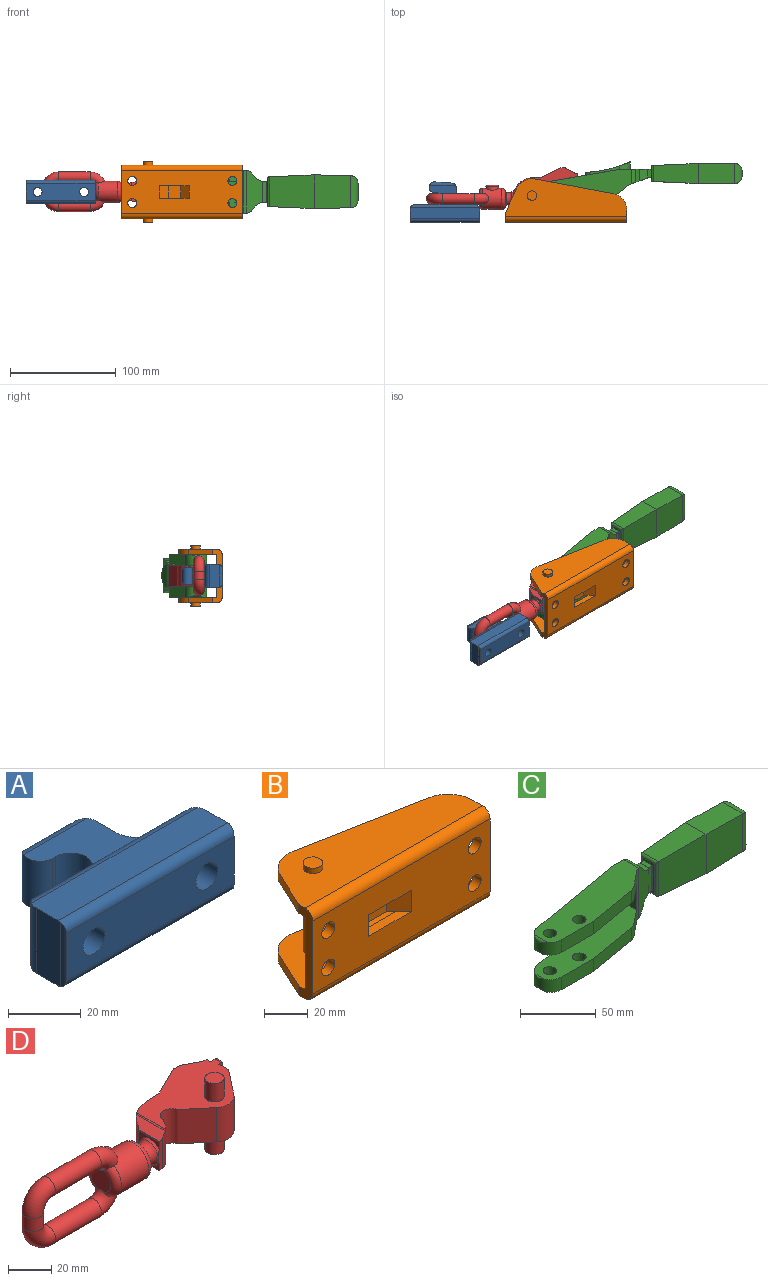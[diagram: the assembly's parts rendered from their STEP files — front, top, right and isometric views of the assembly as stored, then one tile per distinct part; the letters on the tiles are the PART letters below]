
ASSEMBLY  parts=4 mates=3
PART A: 33 faces, bbox 66x38x22 mm
  f0: cylinder r=5mm len=16mm, axis (0,0,1), area 241.4mm2, adj f1,f20,f24,f28,f29,f30
  f1: cylinder r=3mm len=24.58mm, axis (1,0,0), area 67.6mm2, adj f0,f2,f20,f30
  f2: cylinder r=5mm len=16mm, axis (0,0,1), area 117.4mm2, adj f1,f20,f23,f28,f29,f30
  f3: cylinder r=3mm len=64.66mm, axis (1,0,0), area 220mm2, adj f4,f7,f9,f14,f15,f25,f26,f30
  f4: cylinder r=8mm len=19.32mm, axis (0,0,1), area 172.4mm2, adj f3,f5,f15,f16,f22,f23,f28,f30
  f5: cylinder r=3mm len=64.66mm, axis (1,0,0), area 220mm2, adj f4,f8,f9,f14,f22,f25,f26,f28
  f6: cylinder r=3mm len=66mm, axis (1,0,0), area 309.5mm2, adj f7,f10,f11,f12,f13,f21
  f7: plane 66x11mm, normal (0,0,1), area 724.9mm2, adj f3,f6,f9,f12,f13,f14
  f8: plane 66x11mm, normal (0,0,-1), area 724.9mm2, adj f5,f9,f12,f13,f14,f27
  f9: cylinder r=5mm len=22mm, axis (0,0,1), area 162.6mm2, adj f3,f5,f7,f8,f13,f19,f26
  f10: cylinder r=5mm len=21.66mm, axis (0,0,1), area 38.7mm2, adj f6,f11,f13,f27
  f11: plane 65.17x16mm, normal (0,-1,0), area 929.2mm2, adj f6,f10,f17,f21,f27,f31
  f12: plane 22x9.5mm, normal (1,0,0), area 208.9mm2, adj f6,f7,f8,f14,f21,f27
  f13: plane 22x9.5mm, normal (-1,0,0), area 208.9mm2, adj f6,f7,f8,f9,f10,f27
  f14: cylinder r=5mm len=22mm, axis (0,0,1), area 162.6mm2, adj f3,f5,f7,f8,f12,f15,f16,f22
  f15: plane 9x6.57mm, normal (0,1,0), area 33.1mm2, adj f3,f4,f14,f16
  f16: cylinder r=6.75mm len=13.5mm, axis (0,1,0), area 381.7mm2, adj f4,f14,f15,f22,f32
  f17: cylinder r=4.25mm len=8.5mm, axis (0,1,0), area 200.3mm2, adj f11,f18
  f18: plane 13.5x13.5mm, normal (0,1,0), area 86.4mm2, adj f17,f19
  f19: cylinder r=6.75mm len=13.5mm, axis (0,1,0), area 381.7mm2, adj f9,f18,f26
  f20: plane 16x14.49mm, normal (0.06,1,0), area 210.6mm2, adj f0,f1,f2,f29
  f21: cylinder r=5mm len=21.66mm, axis (0,0,1), area 38.7mm2, adj f6,f11,f12,f27
  f22: plane 9x6.57mm, normal (0,1,0), area 33.1mm2, adj f4,f5,f14,f16
  f23: plane 16x7.5mm, normal (1,0,0), area 120mm2, adj f2,f4,f28,f30
  f24: plane 16x1mm, normal (0,-1,0), area 16mm2, adj f0,f25,f28,f30
  f25: cylinder r=6mm len=19.32mm, axis (0,0,1), area 263.9mm2, adj f3,f5,f24,f26,f28,f30
  f26: plane 21.4x19.32mm, normal (0,1,0), area 273.3mm2, adj f3,f5,f9,f19,f25
  f27: cylinder r=3mm len=66mm, axis (1,0,0), area 309.5mm2, adj f8,f10,f11,f12,f13,f21
  f28: plane 31.22x18mm, normal (0,0,-1), area 351.8mm2, adj f0,f2,f4,f5,f23,f24,f25,f29
  f29: cylinder r=3mm len=24.58mm, axis (1,0,0), area 67.6mm2, adj f0,f2,f20,f28
  f30: plane 31.22x18mm, normal (0,0,1), area 351.8mm2, adj f0,f1,f2,f3,f4,f23,f24,f25
  f31: cylinder r=4.25mm len=8.5mm, axis (0,1,0), area 200.3mm2, adj f11,f32
  f32: plane 13.5x13.5mm, normal (0,1,0), area 86.4mm2, adj f16,f31
PART B: 41 faces, bbox 115x41x57 mm
  f0: plane 27.86x5mm, normal (0,0,1), area 114.3mm2, adj f16,f25,f32,f34
  f1: cylinder r=4.5mm len=41mm, axis (0,0,1), area 1159.2mm2, adj f28,f30
  f2: plane 27.86x5mm, normal (0,0,-1), area 114.3mm2, adj f16,f25,f32,f34
  f3: plane 22.55x10.49mm, normal (-0.91,0.42,0), area 124.3mm2, adj f4,f11,f12,f30
  f4: plane 51x9.2mm, normal (-1,0,0), area 286.7mm2, adj f3,f5,f7,f9,f12,f16,f25,f26
  f5: plane 22.55x10.49mm, normal (-0.91,0.42,0), area 124.3mm2, adj f4,f7,f8,f28
  f6: cylinder r=16mm len=15.73mm, axis (0,0,1), area 110.8mm2, adj f7,f10,f15,f28
  f7: plane 115x36mm, normal (0,0,-1), area 3052.2mm2, adj f4,f5,f6,f8,f9,f10,f15,f21
  f8: cylinder r=16mm len=17.46mm, axis (0,0,1), area 105.7mm2, adj f5,f7,f10,f28
  f9: cylinder r=5mm len=115mm, axis (1,0,0), area 903.2mm2, adj f4,f7,f15,f16
  f10: plane 74x13.9mm, normal (0.18,0.98,0), area 376.5mm2, adj f6,f7,f8,f28
  f11: cylinder r=16mm len=17.46mm, axis (0,0,1), area 105.7mm2, adj f3,f12,f13,f30
  f12: plane 115x36mm, normal (0,0,1), area 3052.2mm2, adj f3,f4,f11,f13,f14,f15,f17,f29
  f13: plane 74x13.9mm, normal (0.18,0.98,0), area 376.5mm2, adj f11,f12,f14,f30
  f14: cylinder r=16mm len=15.73mm, axis (0,0,1), area 110.8mm2, adj f12,f13,f15,f30
  f15: plane 51x11.1mm, normal (1,0,0), area 305.7mm2, adj f6,f7,f9,f12,f14,f16,f25,f26
  f16: plane 115x41mm, normal (0,-1,0), area 4153.7mm2, adj f0,f2,f4,f9,f15,f19,f22,f23
  f17: cylinder r=4.5mm len=9mm, axis (0,0,1), area 84.8mm2, adj f12,f18
  f18: plane 9x9mm, normal (0,0,1), area 63.6mm2, adj f17
  f19: cylinder r=4.25mm len=8.5mm, axis (0,1,0), area 133.5mm2, adj f16,f25
  f20: plane 9x9mm, normal (0,0,-1), area 63.6mm2, adj f21
  f21: cylinder r=4.5mm len=9mm, axis (0,0,1), area 84.8mm2, adj f7,f20
  f22: cylinder r=4.25mm len=8.5mm, axis (0,1,0), area 133.5mm2, adj f16,f25
  f23: cylinder r=4.25mm len=8.5mm, axis (0,1,0), area 133.5mm2, adj f16,f25
  f24: cylinder r=4.25mm len=8.5mm, axis (0,1,0), area 133.5mm2, adj f16,f25
  f25: plane 115x39mm, normal (0,1,0), area 3874mm2, adj f0,f2,f4,f15,f19,f22,f23,f24
  f26: cylinder r=1mm len=115mm, axis (1,0,0), area 180.6mm2, adj f4,f15,f25,f28
  f27: cylinder r=1mm len=115mm, axis (1,0,0), area 180.6mm2, adj f4,f15,f25,f30
  f28: plane 115x35mm, normal (0,0,1), area 2937.2mm2, adj f1,f4,f5,f6,f8,f10,f15,f26
  f29: cylinder r=5mm len=115mm, axis (1,0,0), area 903.2mm2, adj f4,f12,f15,f16
  f30: plane 115x35mm, normal (0,0,-1), area 2937.2mm2, adj f1,f3,f4,f11,f13,f14,f15,f27
  f31: plane 12x5.66mm, normal (-0.71,0.71,0), area 96mm2, adj f25,f38,f39,f40
  f32: plane 12x8mm, normal (0.71,-0.71,0), area 135.8mm2, adj f0,f2,f16,f33,f39,f40
  f33: plane 12x11.86mm, normal (0,-1,0), area 142.3mm2, adj f32,f34,f39,f40
  f34: plane 12x8mm, normal (-0.71,-0.71,0), area 135.8mm2, adj f0,f2,f16,f33,f39,f40
  f35: plane 12x5.66mm, normal (0.71,0.71,0), area 96mm2, adj f25,f36,f39,f40
  f36: cylinder r=8mm len=12mm, axis (0,0,1), area 75.4mm2, adj f35,f37,f39,f40
  f37: plane 12x9.37mm, normal (0,1,0), area 112.5mm2, adj f36,f38,f39,f40
  f38: cylinder r=8mm len=12mm, axis (0,0,1), area 75.4mm2, adj f31,f37,f39,f40
  f39: plane 32x8mm, normal (0,0,-1), area 144.7mm2, adj f25,f31,f32,f33,f34,f35,f36,f37
  f40: plane 32x8mm, normal (0,0,1), area 144.7mm2, adj f25,f31,f32,f33,f34,f35,f36,f37
PART C: 68 faces, bbox 209.8x42.8x40.8 mm
  f0: cylinder r=10.5mm len=20.85mm, axis (0,0,1), area 302.1mm2, adj f1,f2,f43,f44,f50,f54
  f1: cylinder r=1mm len=8.94mm, axis (0,1,0), area 7mm2, adj f0,f2
  f2: plane 99x35.5mm, normal (0,0,-1), area 2019.2mm2, adj f0,f1,f3,f7,f12,f39,f40,f41
  f3: plane 20x16.45mm, normal (-1,0,0), area 228.8mm2, adj f2,f4,f10,f12,f39,f58,f65
  f4: plane 99x35.5mm, normal (0,0,1), area 2019.2mm2, adj f3,f5,f9,f10,f39,f51,f52,f53
  f5: cylinder r=1mm len=8.94mm, axis (0,1,0), area 7mm2, adj f4,f52
  f6: plane 14x8mm, normal (-1,0,0), area 112mm2, adj f7,f8,f9,f65
  f7: cylinder r=4mm len=9.21mm, axis (0,-1,0), area 35.5mm2, adj f2,f6,f8,f54,f64,f65,f67
  f8: cylinder r=1mm len=19.29mm, axis (0,0,1), area 26.1mm2, adj f6,f7,f9,f64
  f9: cylinder r=4mm len=9.21mm, axis (0,-1,0), area 35.5mm2, adj f4,f6,f8,f53,f64,f65,f66
  f10: cylinder r=10mm len=13.16mm, axis (0,-1,0), area 102.1mm2, adj f3,f4,f11,f39,f53,f64,f65,f66
  f11: plane 7x2mm, normal (1,0,0), area 14mm2, adj f10,f12,f39,f64
  f12: cylinder r=10mm len=13.16mm, axis (0,-1,0), area 102.1mm2, adj f2,f3,f11,f39,f54,f64,f65,f67
  f13: cylinder r=9.64mm len=11.03mm, axis (0,1,0), area 81.8mm2, adj f14,f39,f48,f59,f60
  f14: plane 8.44x0.17mm, normal (0,0,-1), area 1.4mm2, adj f13,f15,f39,f60
  f15: plane 8.39x3.49mm, normal (0,0,-1), area 28.3mm2, adj f14,f27,f38,f39,f60
  f16: cylinder r=2mm len=15.17mm, axis (0,1,0), area 40.2mm2, adj f17,f28,f37,f38
  f17: plane 42.59x19mm, normal (-0.04,0,-1), area 728.4mm2, adj f16,f18,f30,f36
  f18: plane 34.67x19mm, normal (0.02,0,-1), area 658.9mm2, adj f17,f19,f31,f32,f34,f35
  f19: cylinder r=7mm len=19mm, axis (0,1,0), area 129.9mm2, adj f18,f32,f33,f34
  f20: cylinder r=7mm len=19mm, axis (0,1,0), area 129.9mm2, adj f21,f32,f33,f34
  f21: plane 34.67x19mm, normal (0.02,0,1), area 658.9mm2, adj f20,f22,f31,f32,f34,f35
  f22: plane 42.59x19mm, normal (-0.04,0,1), area 728.4mm2, adj f21,f23,f30,f36
  f23: cylinder r=2mm len=15.17mm, axis (0,1,0), area 40.2mm2, adj f22,f28,f37,f38
  f24: plane 8.39x3.49mm, normal (0,0,1), area 28.3mm2, adj f25,f27,f38,f39,f60
  f25: plane 8.44x0.17mm, normal (0,0,1), area 1.4mm2, adj f24,f26,f39,f60
  f26: cylinder r=9.64mm len=11.03mm, axis (0,1,0), area 81.8mm2, adj f25,f39,f46,f59,f60
  f27: plane 20x0.72mm, normal (-0.04,-1,0), area 14.4mm2, adj f15,f24,f38,f60
  f28: cylinder r=2mm len=28.17mm, axis (0,0,1), area 79.9mm2, adj f16,f23,f30,f38
  f29: cylinder r=10mm len=40.5mm, axis (0,0,1), area 137.2mm2, adj f42,f43,f58,f59
  f30: plane 42.59x32mm, normal (-0.04,-1,0), area 1282.6mm2, adj f17,f22,f28,f31
  f31: plane 34.5x32mm, normal (0,-1,0), area 1075.3mm2, adj f18,f21,f30,f32
  f32: cylinder r=7mm len=30.34mm, axis (0,0,1), area 277.6mm2, adj f18,f19,f20,f21,f31,f33
  f33: plane 16.33x5mm, normal (1,0,0), area 81.7mm2, adj f19,f20,f32,f34
  f34: cylinder r=7mm len=30.34mm, axis (0,0,1), area 277.6mm2, adj f18,f19,f20,f21,f33,f35
  f35: plane 34.5x32mm, normal (0,1,0), area 1075.3mm2, adj f18,f21,f34,f36
  f36: plane 42.59x32mm, normal (-0.04,1,0), area 1282.6mm2, adj f17,f22,f35,f37
  f37: cylinder r=2mm len=28.17mm, axis (0,0,1), area 79.9mm2, adj f16,f23,f36,f38
  f38: plane 24.18x11.18mm, normal (-1,0,0), area 109.7mm2, adj f15,f16,f23,f24,f27,f28,f37,f39
  f39: plane 40.5x29.24mm, normal (0,1,0), area 769.6mm2, adj f2,f3,f4,f10,f11,f12,f13,f14
  f40: cylinder r=4.5mm len=10.25mm, axis (0,0,1), area 289.8mm2, adj f2,f43
  f41: cylinder r=4.5mm len=10.25mm, axis (0,0,1), area 289.8mm2, adj f2,f43
  f42: plane 102.69x35.5mm, normal (0,0,-1), area 2309.6mm2, adj f29,f39,f47,f49,f51,f52,f53,f56
  f43: plane 102.69x35.5mm, normal (0,0,1), area 2309.6mm2, adj f0,f29,f39,f40,f41,f44,f45,f50
  f44: cylinder r=2mm len=12.33mm, axis (0,1,0), area 19.4mm2, adj f0,f43
  f45: cylinder r=6.83mm len=13.77mm, axis (0,1,0), area 62.3mm2, adj f39,f43,f46,f59
  f46: plane 12.35x4.46mm, normal (0.77,0,0.64), area 68.1mm2, adj f26,f39,f45,f59
  f47: cylinder r=6.83mm len=13.77mm, axis (0,1,0), area 62.3mm2, adj f39,f42,f48,f59
  f48: plane 12.35x4.46mm, normal (0.77,0,-0.64), area 68.1mm2, adj f13,f39,f47,f59
  f49: cylinder r=2mm len=12.33mm, axis (0,1,0), area 19.4mm2, adj f42,f52
  f50: plane 30x10.25mm, normal (0,-1,0), area 307.5mm2, adj f0,f2,f43,f55
  f51: plane 30x10.25mm, normal (0,-1,0), area 307.5mm2, adj f4,f42,f52,f56
  f52: cylinder r=10.5mm len=20.85mm, axis (0,0,1), area 302.1mm2, adj f4,f5,f42,f49,f51,f53
  f53: plane 85.56x14.68mm, normal (-0.17,0.99,0), area 858mm2, adj f4,f9,f10,f39,f42,f52,f66
  f54: plane 85.56x14.68mm, normal (-0.17,0.99,0), area 858mm2, adj f0,f2,f7,f12,f39,f43,f67
  f55: plane 42.95x10.25mm, normal (0.17,-0.99,0), area 446.6mm2, adj f2,f43,f50,f57
  f56: plane 42.95x10.25mm, normal (0.17,-0.99,0), area 446.6mm2, adj f4,f42,f51,f63
  f57: cylinder r=10mm len=10.25mm, axis (0,0,1), area 52.1mm2, adj f2,f43,f55,f58
  f58: plane 40.5x12.9mm, normal (0.63,-0.78,0), area 363.4mm2, adj f2,f3,f4,f29,f42,f43,f57,f63
  f59: plane 40.76x15.84mm, normal (0.33,-0.94,0), area 490.2mm2, adj f13,f26,f29,f42,f43,f45,f46,f47
  f60: cylinder r=10mm len=20.02mm, axis (0,0,1), area 67.8mm2, adj f13,f14,f15,f24,f25,f26,f27,f59
  f61: cylinder r=4.5mm len=10.25mm, axis (0,0,1), area 289.8mm2, adj f4,f42
  f62: cylinder r=4.5mm len=10.25mm, axis (0,0,1), area 289.8mm2, adj f4,f42
  f63: cylinder r=10mm len=10.25mm, axis (0,0,1), area 52.1mm2, adj f4,f42,f56,f58
  f64: cylinder r=120mm len=41.5mm, axis (0,0,1), area 893.5mm2, adj f7,f8,f9,f10,f11,f12,f66,f67
  f65: plane 39.1x20.1mm, normal (0.16,-0.99,0), area 784.4mm2, adj f2,f3,f4,f6,f7,f9,f10,f12
  f66: plane 28.5x8.13mm, normal (0,0,-1), area 60.7mm2, adj f9,f10,f53,f64
  f67: plane 28.5x8.13mm, normal (0,0,1), area 60.7mm2, adj f7,f12,f54,f64
PART D: 70 faces, bbox 149.2x40.4x40.6 mm
  f0: torus R=10mm, axis (0,-1,0), area 491.1mm2, adj f2,f68
  f1: torus R=10mm, axis (0,1,0), area 491.3mm2, adj f2,f67
  f2: cylinder r=5mm len=10mm, axis (0,0,1), area 235.6mm2, adj f0,f1
  f3: cylinder r=4.5mm len=10.5mm, axis (0,0,1), area 296.9mm2, adj f4,f51
  f4: plane 9x9mm, normal (0,0,1), area 63.6mm2, adj f3
  f5: cylinder r=4.5mm len=10.5mm, axis (0,0,1), area 296.9mm2, adj f23,f69
  f6: torus R=6.5mm, axis (1,0,0), area 111.9mm2, adj f7,f10,f11,f66
  f7: cylinder r=10mm len=20mm, axis (-1,0,0), area 912.5mm2, adj f6,f8,f9,f11,f12,f66
  f8: torus R=6.5mm, axis (1,0,0), area 111.9mm2, adj f7,f10,f11,f66
  f9: torus R=6.5mm, axis (1,0,0), area 301.5mm2, adj f7,f24
  f10: plane 13x12.53mm, normal (-1,0,0), area 128.2mm2, adj f6,f8,f11,f66
  f11: torus R=10mm, axis (0,1,0), area 342.4mm2, adj f6,f7,f8,f10,f67
  f12: cylinder r=6.2mm len=12.4mm, axis (0,1,0), area 100.3mm2, adj f7,f13
  f13: torus R=3.92mm, axis (0,-1,0), area 94.1mm2, adj f12,f14
  f14: plane 7.83x7.83mm, normal (0,1,0), area 28.6mm2, adj f13,f65
  f15: plane 16.04x13.81mm, normal (-1,0,0), area 70.1mm2, adj f16,f22,f28,f30,f31
  f16: cone r=6.55mm half-angle=20deg, axis (1,0,0), area 55mm2, adj f15,f22,f26,f54
  f17: cylinder r=4mm len=19.65mm, axis (0,1,0), area 17mm2, adj f21,f23,f29,f32
  f18: cylinder r=2mm len=4mm, axis (0,1,0), area 6.8mm2, adj f23,f43,f44,f45,f52,f53
  f19: cylinder r=2mm len=4mm, axis (0,1,0), area 6.8mm2, adj f43,f44,f45,f51,f52,f53
  f20: cylinder r=4mm len=19.65mm, axis (0,1,0), area 17mm2, adj f21,f27,f32,f51
  f21: cylinder r=16mm len=19.5mm, axis (0,0,1), area 261.6mm2, adj f17,f20,f22,f23,f27,f29,f50,f51
  f22: plane 17.45x3.47mm, normal (0.31,-0.95,0), area 52.5mm2, adj f15,f16,f21,f27,f28,f29,f30,f54
  f23: plane 56.36x38.08mm, normal (0,0,-1), area 1227mm2, adj f5,f17,f18,f21,f32,f33,f34,f35
  f24: plane 13x13mm, normal (1,0,0), area 10mm2, adj f9,f25
  f25: cylinder r=6.25mm len=12.5mm, axis (-1,0,0), area 21.6mm2, adj f24,f26
  f26: torus R=10.5mm, axis (1,0,0), area 208.8mm2, adj f16,f25,f54
  f27: plane 21.96x6.54mm, normal (-0.22,0,0.98), area 110.1mm2, adj f20,f21,f22,f28,f31,f32
  f28: cylinder r=2.5mm len=14.09mm, axis (0,1,0), area 7.5mm2, adj f15,f22,f27,f31
  f29: plane 21.96x6.54mm, normal (-0.22,0,-0.98), area 110.1mm2, adj f17,f21,f22,f30,f31,f32
  f30: cylinder r=2.5mm len=14.09mm, axis (0,1,0), area 7.5mm2, adj f15,f22,f29,f31
  f31: cylinder r=5mm len=17.22mm, axis (0,0,1), area 54.9mm2, adj f15,f27,f28,f29,f30,f32
  f32: cylinder r=17mm len=19.5mm, axis (0,0,1), area 346.2mm2, adj f17,f20,f23,f27,f29,f31,f33,f51
  f33: plane 19.5x9.52mm, normal (-0.06,1,0), area 185.9mm2, adj f23,f32,f34,f51
  f34: cylinder r=0.8mm len=19.5mm, axis (0,0,1), area 6.1mm2, adj f23,f33,f35,f51
  f35: plane 19.5x17.86mm, normal (-0.44,0.9,0), area 387.4mm2, adj f23,f34,f36,f51
  f36: cylinder r=2mm len=19.5mm, axis (0,0,1), area 17.7mm2, adj f23,f35,f37,f51
  f37: plane 19.5x3.39mm, normal (0,1,0), area 66mm2, adj f23,f36,f38,f51
  f38: cylinder r=2mm len=19.5mm, axis (0,0,1), area 19.1mm2, adj f23,f37,f39,f51
  f39: plane 19.5x8.69mm, normal (0.47,0.88,0), area 192mm2, adj f23,f38,f40,f51
  f40: cylinder r=2mm len=19.5mm, axis (0,0,1), area 19.1mm2, adj f23,f39,f41,f51
  f41: plane 19.5x1.9mm, normal (0,1,0), area 37.1mm2, adj f23,f40,f42,f51
  f42: plane 19.5x2.88mm, normal (1,0,0), area 56.2mm2, adj f23,f41,f43,f51
  f43: plane 19.5x4.1mm, normal (0,1,0), area 79.7mm2, adj f18,f19,f23,f42,f51,f52
  f44: plane 18.03x3mm, normal (1,0,0), area 54.1mm2, adj f18,f19,f52,f53
  f45: plane 19.5x2.7mm, normal (0,-1,0), area 52.4mm2, adj f18,f19,f23,f46,f51,f53
  f46: plane 19.5x6.48mm, normal (1,0,0), area 126.4mm2, adj f23,f45,f47,f51
  f47: plane 19.5x16.14mm, normal (0.79,-0.62,0), area 399.7mm2, adj f23,f46,f48,f51
  f48: cylinder r=9.08mm len=19.5mm, axis (0,0,1), area 284.3mm2, adj f23,f47,f49,f51
  f49: plane 19.5x13.71mm, normal (-0.64,-0.77,0), area 349mm2, adj f23,f48,f50,f51
  f50: cylinder r=5.5mm len=19.5mm, axis (0,0,1), area 295.5mm2, adj f21,f23,f49,f51
  f51: plane 56.36x38.08mm, normal (0,0,1), area 1227mm2, adj f3,f19,f20,f21,f32,f33,f34,f35
  f52: plane 18.94x0.54mm, normal (0.71,0.71,0), area 13.1mm2, adj f18,f19,f43,f44
  f53: plane 18.94x0.54mm, normal (0.71,-0.71,0), area 13.1mm2, adj f18,f19,f44,f45
  f54: cylinder r=2mm len=5.41mm, axis (0,0,1), area 3.9mm2, adj f16,f22,f26
  f55: plane 3.61x1.73mm, normal (-0.05,0,1), area 6.3mm2, adj f56,f57,f61,f62
  f56: plane 3.46x3.09mm, normal (0,1,0), area 7.8mm2, adj f55,f57,f58,f59,f60,f61
  f57: plane 3.61x1.54mm, normal (-0.89,0,0.45), area 6.3mm2, adj f55,f56,f58,f62
  f58: plane 3.61x1.45mm, normal (-0.84,0,-0.54), area 6.3mm2, adj f56,f57,f59,f62
  f59: plane 3.61x1.73mm, normal (0.05,0,-1), area 6.3mm2, adj f56,f58,f60,f62
  f60: plane 3.61x1.54mm, normal (0.89,0,-0.45), area 6.3mm2, adj f56,f59,f61,f62
  f61: plane 3.61x1.45mm, normal (0.84,0,0.54), area 6.3mm2, adj f55,f56,f60,f62
  f62: plane 4x4mm, normal (0,1,0), area 4.8mm2, adj f55,f57,f58,f59,f60,f61,f63
  f63: cylinder r=2mm len=4mm, axis (0,1,0), area 12.6mm2, adj f62,f64
  f64: plane 5x5mm, normal (0,1,0), area 7.1mm2, adj f63,f65
  f65: cylinder r=2.5mm len=5mm, axis (0,1,0), area 15.7mm2, adj f14,f64
  f66: torus R=10mm, axis (0,-1,0), area 342.5mm2, adj f6,f7,f8,f10,f68
  f67: cylinder r=5mm len=30.3mm, axis (-1,0,0), area 949.8mm2, adj f1,f11
  f68: cylinder r=5mm len=30.3mm, axis (-1,0,0), area 949.8mm2, adj f0,f66
  f69: plane 9x9mm, normal (0,0,-1), area 63.6mm2, adj f5
PLACE A t=(-65.33,42.91,2.77)mm
PLACE B t=(25.25,42.91,2.77)mm fixed
PLACE C rot(axis=(0,0,-1),0deg) t=(50.25,67.91,3.02)mm
PLACE D rot(axis=(-0.8,-0.55,-0.24),0deg) t=(75.12,65.3,3.02)mm
MATE revolute D.f3 <-> C.f40  axis (0,0,1) through (75.12,65.3,23.27)mm
MATE revolute C.f41 <-> B.f1  axis (0,0,1) through (50.25,67.91,23.27)mm
MATE fastened B.f16 <-> A.f11  axis (0,-1,0) through (25.25,42.91,2.77)mm
